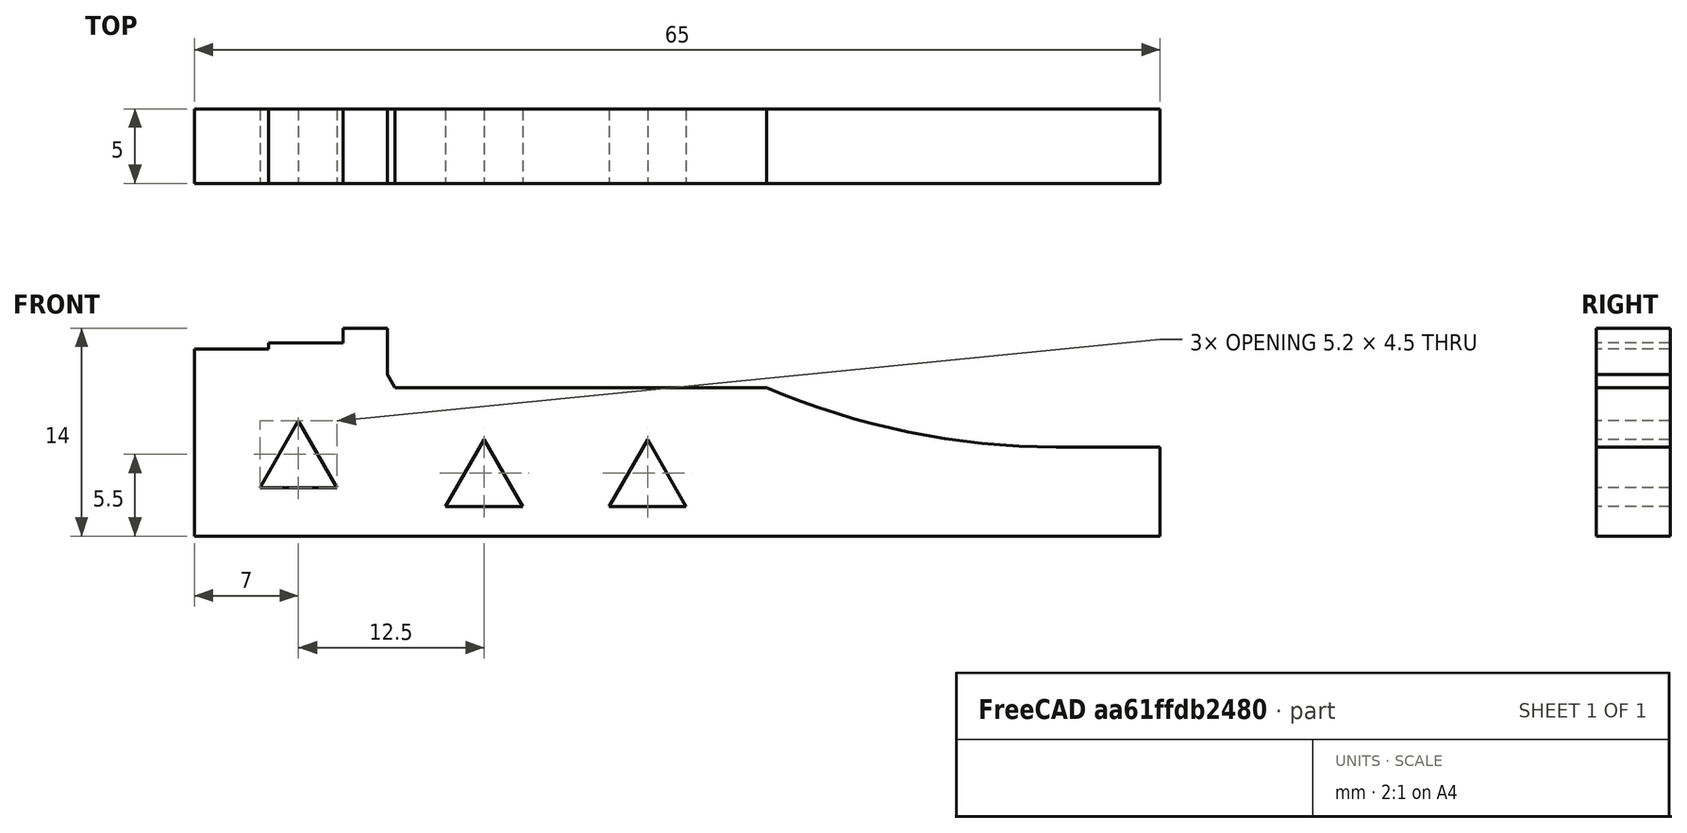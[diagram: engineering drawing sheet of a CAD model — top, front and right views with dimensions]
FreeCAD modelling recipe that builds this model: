
FCSTD DOCUMENT  (FreeCAD 1.1R41628 (Git))
Label: cartoheightwscale
License: All rights reserved
LicenseURL: https://en.wikipedia.org/wiki/All_rights_reserved
objects: Sketcher::SketchObject×2, App::Point×1, PartDesign::Pad×1, App::VarSet×1, PartDesign::Body×1
note: 8 computed .brp shape members not serialized (recipe doc carries the construction recipe); baked Part::Feature solids carry a one-line shape summary decoded from their .brp

FEATURE [App::Point] Origin001
  Role = Origin
FEATURE [Sketcher::SketchObject] Sketch
  ArcFitTolerance = 1e-06
  AttachmentSupport = -> [XZ_Plane]
  ExternalTypes = [0]
  FullyConstrained = true
  MakeInternals = false
  MapMode = 5
  Placement = pos=(0,0,0) rot=(1,0,0;1.5708rad)
  expr: Constraints[48] = VarSet.Height_High
  expr: Constraints[49] = VarSet.Height_Low
  sketch-geometry (25):
    g0: LineSegment StartX=0 StartY=0 StartZ=0 EndX=0 EndY=6 EndZ=0
    g1: LineSegment StartX=-55 StartY=14 StartZ=0 EndX=-55 EndY=13 EndZ=0
    g2: LineSegment StartX=-55 StartY=13 StartZ=0 EndX=-60 EndY=13 EndZ=0
    g3: LineSegment StartX=-60 StartY=13 StartZ=0 EndX=-60 EndY=12.6 EndZ=0
    g4: LineSegment StartX=-60 StartY=12.6 StartZ=0 EndX=-65 EndY=12.6 EndZ=0
    g5: LineSegment StartX=-65 StartY=12.6 StartZ=0 EndX=-65 EndY=0 EndZ=0
    g6: LineSegment StartX=-65 StartY=0 StartZ=0 EndX=0 EndY=0 EndZ=0
    g7: LineSegment StartX=-51.5 StartY=10 StartZ=0 EndX=-26.5 EndY=10 EndZ=0
    g8: LineSegment StartX=0 StartY=6 StartZ=0 EndX=-7 EndY=6 EndZ=0
    g9: ArcOfCircle CenterX=-7 CenterY=55.5312 CenterZ=0 NormalX=0 NormalY=0 NormalZ=1 AngleXU=0 Radius=49.5312 StartAngle=4.30775 EndAngle=4.71239
    g10: LineSegment StartX=-42.9019 StartY=2 StartZ=0 EndX=-45.5 EndY=6.5 EndZ=0
    g11: LineSegment StartX=-45.5 StartY=6.5 StartZ=0 EndX=-48.0981 EndY=2 EndZ=0
    g12: LineSegment StartX=-48.0981 StartY=2 StartZ=0 EndX=-42.9019 EndY=2 EndZ=0
    g13: Circle [constr] CenterX=-45.5 CenterY=3.5 CenterZ=0 NormalX=0 NormalY=0 NormalZ=1 AngleXU=0 Radius=3
    g14: LineSegment StartX=-34.5 StartY=6.5 StartZ=0 EndX=-37.0981 EndY=2 EndZ=0
    g15: LineSegment StartX=-37.0981 StartY=2 StartZ=0 EndX=-31.9019 EndY=2 EndZ=0
    g16: LineSegment StartX=-31.9019 StartY=2 StartZ=0 EndX=-34.5 EndY=6.5 EndZ=0
    g17: Circle [constr] CenterX=-34.5 CenterY=3.5 CenterZ=0 NormalX=0 NormalY=0 NormalZ=1 AngleXU=0 Radius=3
    g18: LineSegment StartX=-55 StartY=14 StartZ=0 EndX=-52 EndY=14 EndZ=0
    g19: LineSegment StartX=-52 StartY=10.866 StartZ=0 EndX=-52 EndY=14 EndZ=0
    g20: LineSegment StartX=-52 StartY=10.866 StartZ=0 EndX=-51.5 EndY=10 EndZ=0
    g21: LineSegment StartX=-55.4019 StartY=3.25 StartZ=0 EndX=-58 EndY=7.75 EndZ=0
    g22: LineSegment StartX=-58 StartY=7.75 StartZ=0 EndX=-60.5981 EndY=3.25 EndZ=0
    g23: LineSegment StartX=-60.5981 StartY=3.25 StartZ=0 EndX=-55.4019 EndY=3.25 EndZ=0
    g24: Circle [constr] CenterX=-58 CenterY=4.75 CenterZ=0 NormalX=0 NormalY=0 NormalZ=1 AngleXU=0 Radius=3
  constraints (74):
    c: Vertical(g0)
    c: Vertical(g1)
    c: Coincident(g1,g2)
    c: Horizontal(g2)
    c: Coincident(g2,g3)
    c: Vertical(g3)
    c: Coincident(g3,g4)
    c: Horizontal(g4)
    c: Coincident(g4,g5)
    c: PointOnObject(g5,g-1)
    c: Vertical(g5)
    c: Coincident(g5,g6)
    c: Coincident(g6,g0)
    c: Coincident(g0,g-1)
    c: DistanceX(g4,g4) = 5
    c: DistanceY(g0,g0) = 6
    c: Horizontal(g7)
    c: Coincident(g8,g0)
    c: Horizontal(g8)
    c: Coincident(g9,g7)
    c: Tangent(g9,g8) = 1.5708
    c: DistanceX(g8,g8) = 7
    c: DistanceX(g7,g7) = 25
    c: DistanceX(g2,g2) = 5
    c: Coincident(g10,g11)
    c: Coincident(g11,g12)
    c: Coincident(g12,g10)
    c: Equal(g10,g11)
    c: Equal(g10,g12)
    c: PointOnObject(g10,g13)
    c: PointOnObject(g11,g13)
    c: PointOnObject(g12,g13)
    c: Horizontal(g12)
    c: Coincident(g14,g15)
    c: Coincident(g15,g16)
    c: Coincident(g16,g14)
    c: Equal(g14,g15)
    c: Equal(g14,g16)
    c: PointOnObject(g14,g17)
    c: PointOnObject(g15,g17)
    c: PointOnObject(g16,g17)
    c: Equal(g13,g17)
    c: Diameter(g13) = 6
    c: Horizontal(g15)
    c: DistanceY(g-1,g7) = 10
    c: Coincident(g18,g1)
    c: Horizontal(g18)
    c: Coincident(g19,g18)
    c: DistanceY(g7,g1) = 3
    c: DistanceY(g7,g3) = 2.6
    c: DistanceX(g18,g18) = 3
    c: DistanceY(g1,g1) = 1
    c: DistanceX(g5,g0) = 65
    c: Vertical(g19)
    c: Coincident(g20,g19)
    c: Coincident(g20,g7)
    c: Coincident(g21,g22)
    c: Coincident(g22,g23)
    c: Coincident(g23,g21)
    c: Equal(g21,g22)
    c: Equal(g21,g23)
    c: PointOnObject(g21,g24)
    c: PointOnObject(g22,g24)
    c: PointOnObject(g23,g24)
    c: Horizontal(g13,g17)
    c: DistanceX(g13,g17) = 11
    c: Angle(g7,g20) = 2.0944
    c: DistanceX(g20,g20) = 0.5
    c: Horizontal(g22,g21)
    c: Equal(g24,g13)
    c: DistanceX(g24,g13) = 12.5
    c: DistanceY(g5,g24) = 4.75
    c: DistanceY(g5,g13) = 3.5
    c: DistanceX(g5,g24) = 7
FEATURE [PartDesign::Pad] Pad
  Direction = (0,-1,2e-16)
  Length = 5
  Length2 = 10
  Midplane = true
  Placement = pos=(0,0,0) rot=(1,0,0;1.5708rad)
  Profile = -> Sketch
  ReferenceAxis = -> Sketch [N_Axis]
  Suppressed = false
  Type = 0
FEATURE [App::VarSet] VarSet
  Height_High = 3
  Height_Low = 2.6
  Offset_Mark = 18.665
FEATURE [Sketcher::SketchObject] Sketch001
  ArcFitTolerance = 1e-06
  AttachmentOffset = pos=(0,0,10) rot=(0,0,1;0rad)
  AttachmentSupport = -> [XY_Plane]
  ExternalGeometry = -> [Pad]
  ExternalTypes = [0]
  FullyConstrained = true
  MakeInternals = false
  MapMode = 5
  Placement = pos=(0,0,10) rot=(0,0,1;0rad)
  expr: Constraints[8] = VarSet.Offset_Mark
  sketch-geometry (4):
    g0: Circle [constr] CenterX=-68.8 CenterY=0 CenterZ=0 NormalX=0 NormalY=0 NormalZ=1 AngleXU=0 Radius=1.64
    g1: LineSegment StartX=-49.702 StartY=-2.75 StartZ=0 EndX=-50.135 EndY=-2 EndZ=0
    g2: LineSegment StartX=-50.135 StartY=-2 StartZ=0 EndX=-50.568 EndY=-2.75 EndZ=0
    g3: LineSegment StartX=-50.568 StartY=-2.75 StartZ=0 EndX=-49.702 EndY=-2.75 EndZ=0
  constraints (12):
    c: PointOnObject(g0,g-1)
    c: Radius(g0) = 1.64
    c: Coincident(g1,g2)
    c: Coincident(g2,g3)
    c: Coincident(g3,g1)
    c: Equal(g1,g2)
    c: Equal(g1,g3)
    c: Horizontal(g3)
    c: DistanceX(g0,g1) = 18.665
    c: DistanceY(g1,g1) = 0.75
    c: DistanceX(g0,g-3) = 8.8
    c: DistanceY(g-3,g1) = 0.5
FEATURE [PartDesign::Body] Body  label="Gauge"
  AllowCompound = false
  Group = -> [Sketch,Pad,Sketch001]
  Origin = -> Origin
  Tip = -> Pad
